# Revit family: 67L-W-SQ
name_source: partatom
category: Lighting Fixtures
revit_build: Autodesk Revit 2014 (Build: 20130308_1515(x64)
units: mm (PartAtom-declared; Revit-internal decimal feet)

## types (6) — shared parameters
Apparent Load = 5 VA
Assembly Code = D5020210
Color Filter = 16777215
Description = The NOTE 67L Wall Mount brings direct illumination, ADA compliance, performance and versatility, all within a slim profile and a fresh, contemporary style
Dimming Lamp Color Temperature Shift = <None>
Emit Shape Visible in Rendering = No
Emit from Rectangle Length = 3 "
Emit from Rectangle Width = 47 "
Glass = Hubbell - White Glass
Lamp = LED
Load Classification = Lighting
Manufacturer = Litecontrol
Model = 67L-W-Square
Photometric Link = https://resources.hubbelllighting.com
Photometric Notes = Photometric Web files Download in below link
Photometric Web File = 67L-W-D-4-4-DM-C1-35K-D055.IES
Power Factor = 1
Product Documentation Link = https://hubbellcdn.com
Product Page URL = https://www.hubbell.com
Tilt Angle = 0.00°
Type Comments = Lighting Fixture
URL = https://www.hubbell.com
Voltage = 120 V
Wattage Comments = 550 to 1800 lumens/ft
Watts = 5 W
Width = 48 "

## per-type parameters (varying)
| type | Housing Material |
| Note 67L-Carbon Black | Paint - Hubbell - Carbon Black |
| Note 67L-Textured Matte White | Paint - Hubbell - Textured Matte White |
| Note 67L-Light Silver | Paint - Hubbell - Light Silver |
| Note 67L-Machined Aluminum | Paint - Hubbell - Machined Aluminum |
| Note 67L-Textured Camera Black | Paint - Hubbell - Textured Camera Black |
| Note 67L-Matte White | Paint - Hubbell - Matte White |

## geometry (parser evidence)
native form markers: Blend x6, Sweep x4
no freeform markers — native parametric forms only
